# Revit family: Shower-Valve_Trim-KALLISTA-Vice-P34604
name_source: partatom
category: Specialty Equipment
units: mm (PartAtom-declared; Revit-internal decimal feet)

## family parameters
Cut with Voids When Loaded = No
Host = Face
OmniClass Number = 23.31.25.00
OmniClass Title = Toilet and Bath Specialties
Part Type = Normal
Room Calculation Point = No
Round Connector Dimension = Use Diameter
Shared = No

## types (5) — shared parameters
ADA Compliant = No
Date Modified = 05/27/2024
Default Elevation = 42"
Description = Industrial Pressure Balance Trim With Diverter
Drain Included = No
Handle Clearance = 3 1/8"
Height = 6 1/2"
Length = 5 13/16"
Manufacturer = Kallista Co.
Master Format 2014 = 10 28 00
Master Format 2014 Name = Toilet, Bath, and Laundry Accessories
Material = Premium Metal Construction
Product Name = Vice
URL = https://www.kallista.com
WaterSense Certified = No
Width = 6 1/2"

## per-type parameters (varying)
| type | Assembly Code | Finish | Model | Secondary Finish | Type |
| Bruhsed Bronze, CP-Chrome | D2010700 | Kallista-Metal-CP-Chrome | P34604-BV-CP | Kallista-Metal-BV-Brushed_Bronze | 4 |
| Bruhsed French Gold, AF-French Gold | C1030200 | Kallista-Metal-AF-French_Gold | P34604-BAF-AF | Kallista-Metal-BAF-Brushed_French_Gold | 1 |
| Chrome, CP-Chrome | D2010700 | Kallista-Metal-CP-Chrome | P34604-CP-CP | Kallista-Metal-CP-Chrome | 5 |
| Vibrant Bruhsed Nickel, BGP | D2010700 | Kallista-Metal-BGP | P34604-BN-BGP | Kallista-Metal-BN-Brushed_Nickel | 2 |
| Vibrant Bruhsed Nickel, SN-Polished Nickel | D2010700 | Kallista-Metal-SN-Polished_Nickel | P34604-BN-SN | Kallista-Metal-BN-Brushed_Nickel | 3 |

## geometry (parser evidence)
native form markers: Sweep x5
no freeform markers — native parametric forms only
